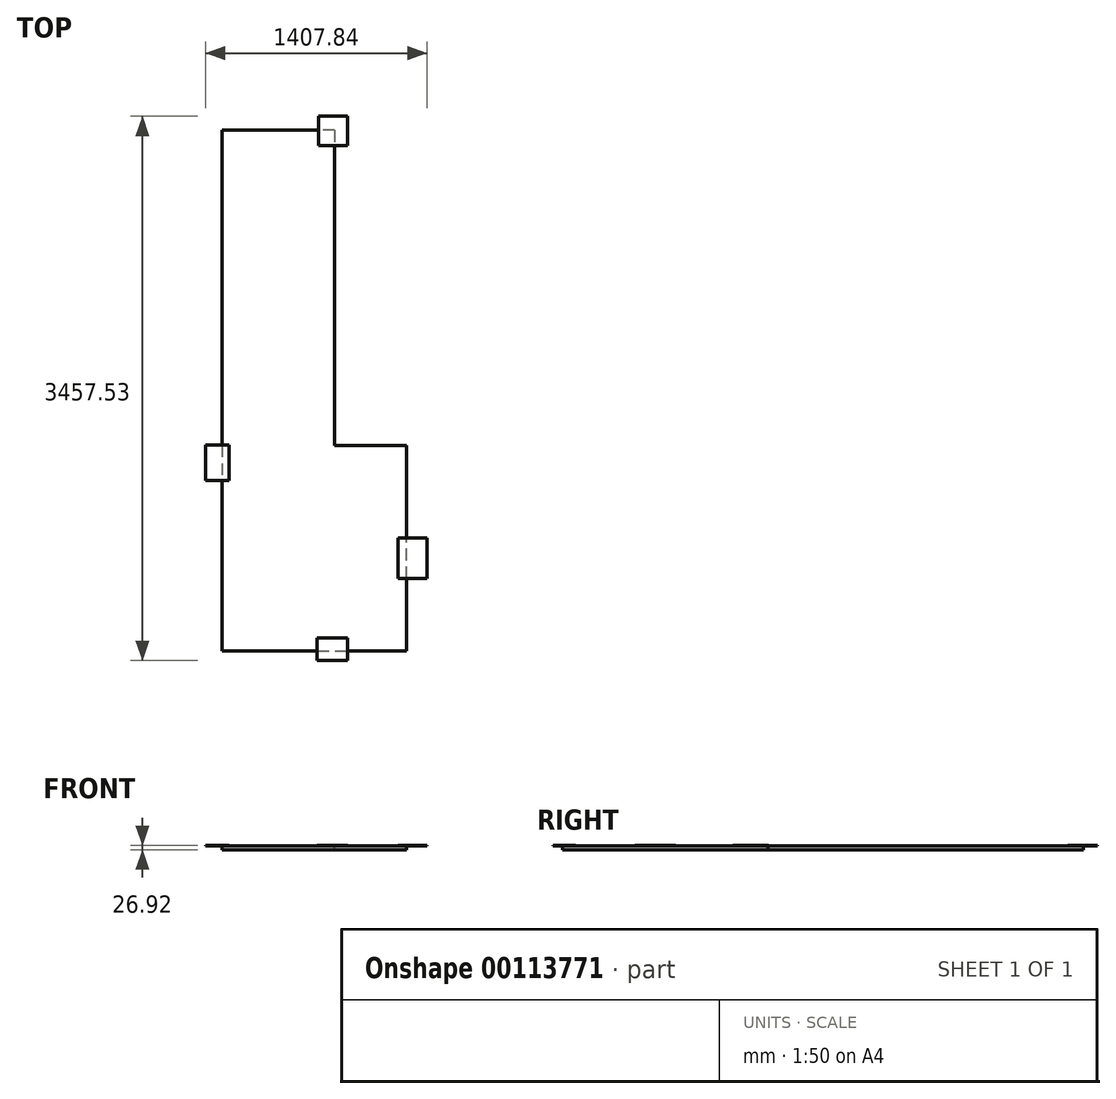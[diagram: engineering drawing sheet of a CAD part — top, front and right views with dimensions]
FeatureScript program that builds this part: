
annotation { "Feature Type Name" : "Feature", "Feature Type Description" : "" }
export const myFeature = defineFeature(function(context is Context, id is Id, definition is map)
    precondition{}
    {
        {
            var Q0;
            Q0=qCreatedBy(makeId("Top.planeOp"),FACE);
            var sketch = newSketch(context, id + "F0", { "sketchPlane" : qUnion([Q0])});
            skLineSegment(sketch, "E0.bottom", {"start": v(1943.1, -1803.4) * mm, "end": v(-1943.1, -1803.4) * mm, "construction": true});
            skLineSegment(sketch, "E0.top", {"start": v(1943.1, 1498.6) * mm, "end": v(-1943.1, 1498.6) * mm, "construction": true});
            skLineSegment(sketch, "E0.left", {"start": v(1943.1, -1803.4) * mm, "end": v(1943.1, 1498.6) * mm, "construction": true});
            skLineSegment(sketch, "E0.right", {"start": v(-1943.1, -1803.4) * mm, "end": v(-1943.1, 1498.6) * mm, "construction": true});
            skPoint(sketch, "E0.middle", {"position": v(0, -152.4) * mm});
            skLineSegment(sketch, "E1", {"start": v(0, 644.85) * mm, "end": v(0, 316.8) * mm, "construction": true});
            skLineSegment(sketch, "E2", {"start": v(-2123.45, 0) * mm, "end": v(1678.64, 0) * mm, "construction": true});
            skSolve(sketch);
        }
        {
            var Q0;
            Q0=qCreatedBy(makeId("Top.planeOp"),FACE);
            var sketch = newSketch(context, id + "F1", { "sketchPlane" : qUnion([Q0])});
            skLineSegment(sketch, "E3.bottom", {"start": v(-1850.34, -1865.77) * mm, "end": v(-2044.6, -1865.77) * mm});
            skLineSegment(sketch, "E3.top", {"start": v(-1850.34, -1721.65) * mm, "end": v(-2044.6, -1721.65) * mm});
            skLineSegment(sketch, "E3.left", {"start": v(-1850.34, -1865.77) * mm, "end": v(-1850.34, -1721.65) * mm});
            skLineSegment(sketch, "E3.right", {"start": v(-2044.6, -1865.77) * mm, "end": v(-2044.6, -1721.65) * mm});
            skPoint(sketch, "E3.middle", {"position": v(-1947.47, -1793.7) * mm});
            skLineSegment(sketch, "E4.0", {"start": v(-1943.1, -1803.4) * mm, "end": v(-1943.1, 1498.6) * mm, "construction": true});
            skLineSegment(sketch, "E5.0", {"start": v(1943.1, 1498.6) * mm, "end": v(-1943.1, 1498.6) * mm, "construction": true});
            skLineSegment(sketch, "E6.0", {"start": v(1943.1, -1803.4) * mm, "end": v(1943.1, 1498.6) * mm, "construction": true});
            skLineSegment(sketch, "E7.0", {"start": v(1943.1, -1803.4) * mm, "end": v(-1943.1, -1803.4) * mm, "construction": true});
            skLineSegment(sketch, "E8.bottom", {"start": v(-2035.3, 1405.44) * mm, "end": v(-1850.9, 1405.44) * mm});
            skLineSegment(sketch, "E8.top", {"start": v(-2035.3, 1591.76) * mm, "end": v(-1850.9, 1591.76) * mm});
            skLineSegment(sketch, "E8.left", {"start": v(-2035.3, 1405.44) * mm, "end": v(-2035.3, 1591.76) * mm});
            skLineSegment(sketch, "E8.right", {"start": v(-1850.9, 1405.44) * mm, "end": v(-1850.9, 1591.76) * mm});
            skPoint(sketch, "E8.middle", {"position": v(-1943.1, 1498.6) * mm});
            skSolve(sketch);
        }
        {
            var Q0;
            Q0 = qSketchRegion(id + "F1", true);
            extrude(context, id + "F2", {"entities" : qUnion([Q0]), "depth" : 1.52 * mm});
        }
        {
            var Q0;
            Q0=qCreatedBy(makeId("Top.planeOp"),FACE);
            var sketch = newSketch(context, id + "F3", { "sketchPlane" : qUnion([Q0])});
            skLineSegment(sketch, "E9.0", {"start": v(-1943.1, -1803.4) * mm, "end": v(-1943.1, 1498.6) * mm, "construction": true});
            skLineSegment(sketch, "E10.0", {"start": v(1943.1, -1803.4) * mm, "end": v(-1943.1, -1803.4) * mm, "construction": true});
            skLineSegment(sketch, "E11.0", {"start": v(-2679.7, 0) * mm, "end": v(1678.64, 0) * mm, "construction": true});
            skLineSegment(sketch, "E12.0", {"start": v(1943.1, 1498.6) * mm, "end": v(-1943.1, 1498.6) * mm, "construction": true});
            skLineSegment(sketch, "E13.0", {"start": v(1943.1, -1803.4) * mm, "end": v(1943.1, 1498.6) * mm, "construction": true});
            skLineSegment(sketch, "E14.0", {"start": v(-2679.7, -1803.4) * mm, "end": v(-2679.7, 1498.6) * mm, "construction": true});
            skPoint(sketch, "E15.orphan", {"position": v(-2123.45, 0) * mm});
            skLineSegment(sketch, "E16.0", {"start": v(-2679.7, -609.6) * mm, "end": v(1678.64, -609.6) * mm, "construction": true});
            skLineSegment(sketch, "E17.bottom", {"start": v(-2605.06, -720.92) * mm, "end": v(-2754.34, -720.92) * mm});
            skLineSegment(sketch, "E17.top", {"start": v(-2605.06, -498.28) * mm, "end": v(-2754.34, -498.28) * mm});
            skLineSegment(sketch, "E17.left", {"start": v(-2605.06, -720.92) * mm, "end": v(-2605.06, -498.28) * mm});
            skLineSegment(sketch, "E17.right", {"start": v(-2754.34, -720.92) * mm, "end": v(-2754.34, -498.28) * mm});
            skPoint(sketch, "E17.middle", {"position": v(-2679.7, -609.6) * mm});
            skSolve(sketch);
        }
        {
            var Q0;
            Q0 = qSketchRegion(id + "F3", true);
            extrude(context, id + "F4", {"entities" : qUnion([Q0]), "depth" : 1.52 * mm});
        }
        {
            var Q0;
            Q0=qCreatedBy(makeId("Top.planeOp"),FACE);
            var sketch = newSketch(context, id + "F5", { "sketchPlane" : qUnion([Q0])});
            skLineSegment(sketch, "E18.0", {"start": v(-1943.1, -1803.4) * mm, "end": v(-1943.1, 1498.6) * mm, "construction": true});
            skLineSegment(sketch, "E19.0", {"start": v(-698.5, -1803.4) * mm, "end": v(-698.5, 1498.6) * mm, "construction": true});
            skLineSegment(sketch, "E20.0", {"start": v(-1530.35, -1803.4) * mm, "end": v(-1530.35, 1498.6) * mm, "construction": true});
            skLineSegment(sketch, "E21.0", {"start": v(-2123.45, -1343.79) * mm, "end": v(1678.64, -1343.79) * mm, "construction": true});
            skLineSegment(sketch, "E22.MirrorCS", {"start": v(-2123.45, 1343.79) * mm, "end": v(1678.64, 1343.79) * mm, "construction": true});
            skLineSegment(sketch, "E23.bottom", {"start": v(-1530.35, -1343.79) * mm, "end": v(-1346.5, -1343.79) * mm});
            skLineSegment(sketch, "E23.top", {"start": v(-1530.35, -1087.87) * mm, "end": v(-1346.5, -1087.87) * mm});
            skLineSegment(sketch, "E23.left", {"start": v(-1530.35, -1343.79) * mm, "end": v(-1530.35, -1087.87) * mm});
            skLineSegment(sketch, "E23.right", {"start": v(-1346.5, -1343.79) * mm, "end": v(-1346.5, -1087.87) * mm});
            skSolve(sketch);
        }
        {
            var Q0;
            Q0 = qSketchRegion(id + "F5", true);
            extrude(context, id + "F6", {"entities" : qUnion([Q0]), "depth" : 1.52 * mm});
        }
        {
            var Q0;
            Q0=makeQuery(id+"F4.opExtrude","CAP_FACE",FACE,{"disambiguationData":[OSD([sQuery(id+"F3.wireOp",EDGE,"E17.bottom"),sQuery(id+"F3.wireOp",EDGE,"E17.top"),sQuery(id+"F3.wireOp",EDGE,"E17.left"),sQuery(id+"F3.wireOp",EDGE,"E17.right")])],"isStart":true});
            var sketch = newSketch(context, id + "F7", { "sketchPlane" : qUnion([Q0])});
            skLineSegment(sketch, "E24.bottom", {"start": v(-1932.68, -1503) * mm, "end": v(-2647.02, -1503) * mm});
            skLineSegment(sketch, "E24.top", {"start": v(-1932.68, 1805.52) * mm, "end": v(-2647.02, 1805.52) * mm});
            skLineSegment(sketch, "E24.left", {"start": v(-1932.68, -1503) * mm, "end": v(-1932.68, 1805.52) * mm});
            skLineSegment(sketch, "E24.right", {"start": v(-2647.02, -1503) * mm, "end": v(-2647.02, 1805.52) * mm});
            skLineSegment(sketch, "E25.bottom", {"start": v(-1932.68, 1805.52) * mm, "end": v(-1477.38, 1805.52) * mm});
            skLineSegment(sketch, "E25.top", {"start": v(-1932.68, 499.58) * mm, "end": v(-1477.38, 499.58) * mm});
            skLineSegment(sketch, "E25.left", {"start": v(-1932.68, 1805.52) * mm, "end": v(-1932.68, 499.58) * mm});
            skLineSegment(sketch, "E25.right", {"start": v(-1477.38, 1805.52) * mm, "end": v(-1477.38, 499.58) * mm});
            skSolve(sketch);
        }
        {
            var Q0;
            Q0 = qSketchRegion(id + "F7", true);
            extrude(context, id + "F8", {"entities" : qUnion([Q0]), "depth" : 25.4 * mm});
        }
    });
